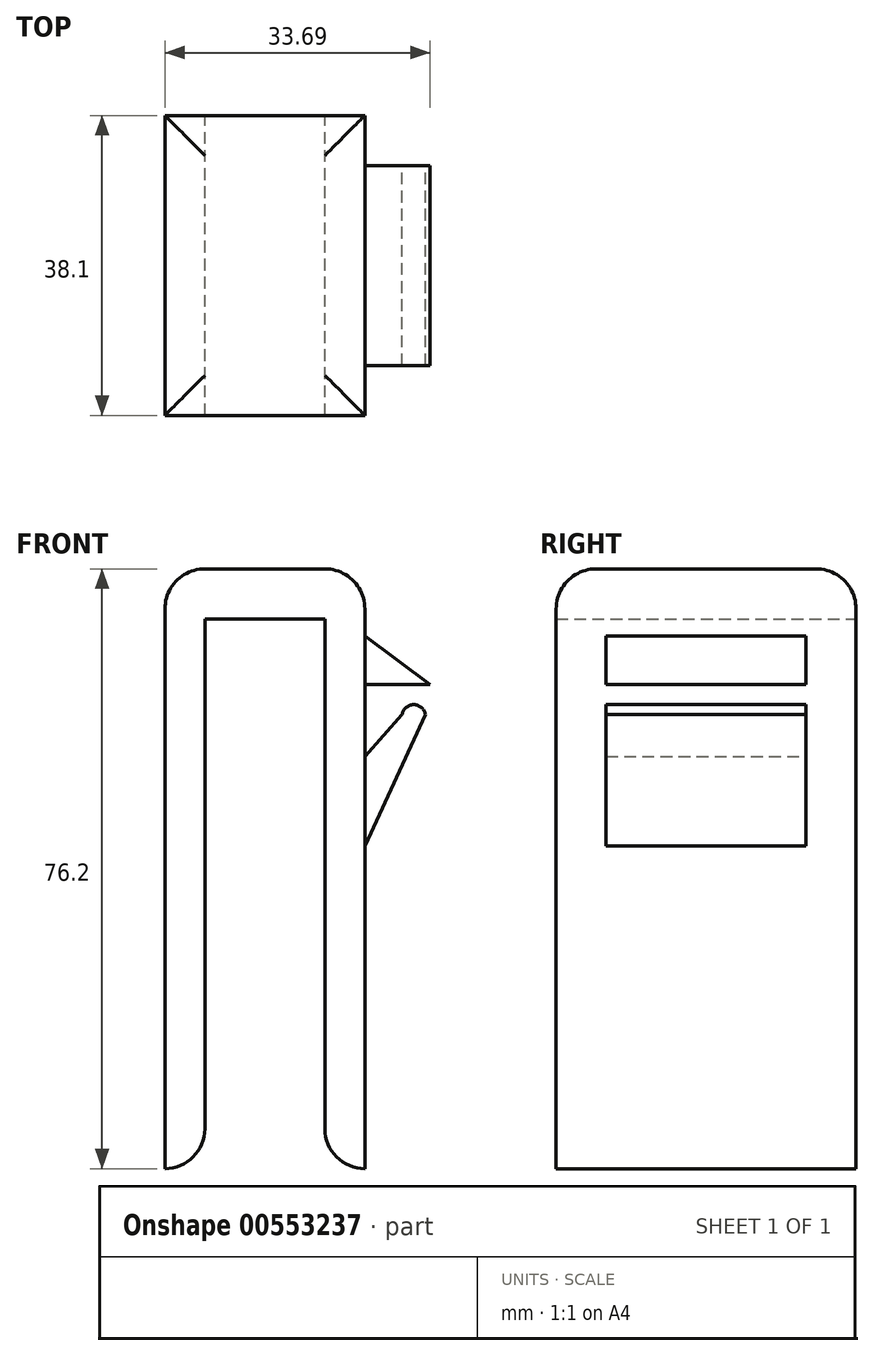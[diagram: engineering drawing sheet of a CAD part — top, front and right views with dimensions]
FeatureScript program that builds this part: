
annotation { "Feature Type Name" : "Feature", "Feature Type Description" : "" }
export const myFeature = defineFeature(function(context is Context, id is Id, definition is map)
    precondition{}
    {
        {
            var Q0;
            Q0=qCreatedBy(makeId("Front.planeOp"),FACE);
            var sketch = newSketch(context, id + "F0", { "sketchPlane" : qUnion([Q0])});
            skLineSegment(sketch, "E0", {"start": v(-8.12, 12.15) * mm, "end": v(7.12, 12.15) * mm});
            skLineSegment(sketch, "E1", {"start": v(-8.12, 12.15) * mm, "end": v(-8.12, -57.7) * mm});
            skLineSegment(sketch, "E2", {"start": v(7.12, 12.15) * mm, "end": v(7.12, -57.7) * mm});
            skLineSegment(sketch, "E3", {"start": v(-8.12, -57.7) * mm, "end": v(-13.2, -57.7) * mm});
            skLineSegment(sketch, "E4", {"start": v(-13.2, -57.7) * mm, "end": v(-13.2, 18.5) * mm});
            skLineSegment(sketch, "E5", {"start": v(-13.2, 18.5) * mm, "end": v(12.2, 18.5) * mm});
            skLineSegment(sketch, "E6", {"start": v(12.2, 18.5) * mm, "end": v(12.2, -57.7) * mm});
            skLineSegment(sketch, "E7", {"start": v(12.2, -57.7) * mm, "end": v(7.12, -57.7) * mm});
            skLineSegment(sketch, "E8", {"start": v(12.2, -5.36) * mm, "end": v(16.92, 0) * mm});
            skLineSegment(sketch, "E9", {"start": v(16.92, 0) * mm, "end": v(19.88, 0) * mm});
            skLineSegment(sketch, "E10", {"start": v(19.88, 0) * mm, "end": v(12.2, -16.68) * mm});
            skLineSegment(sketch, "E11", {"start": v(16.92, 3.81) * mm, "end": v(12.2, 3.8) * mm});
            skLineSegment(sketch, "E12", {"start": v(16.92, 3.8) * mm, "end": v(20.5, 3.8) * mm});
            skLineSegment(sketch, "E13", {"start": v(20.5, 3.81) * mm, "end": v(12.2, 9.99) * mm});
            skArc(sketch, "E14", {"start": v(19.88, 0) * mm, "mid": v(18.4, 1.24) * mm, "end": v(16.92, 0) * mm});
            skSolve(sketch);
        }
        {
            var Q0;
            Q0=makeQuery(id+"F0.imprint","IMPRINT",FACE,{"disambiguationData":[TD([[makeQuery(id+"F0.imprint","IMPRINT",EDGE,{"derivedFrom":sQuery(id+"F0.wireOp",EDGE,"E0")}),1.0]])]});
            extrude(context, id + "F1", {"entities" : qUnion([Q0]), "endBound" : BoundingType.SYMMETRIC, "depth" : 38.1 * mm, "offsetDistance" : 25.4 * mm});
        }
        {
            var Q0;
            {var subQ0=sQuery(id+"F0.wireOp",EDGE,"E11");Q0=makeQuery(id+"F0.imprint","IMPRINT",FACE,{"disambiguationData":[TD([[makeQuery(id+"F0.imprint","IMPRINT",EDGE,{"derivedFrom":subQ0}),-1.0]])]});}
            var Q1;
            {var subQ0=sQuery(id+"F0.wireOp",EDGE,"E8");Q1=makeQuery(id+"F0.imprint","IMPRINT",FACE,{"disambiguationData":[TD([[makeQuery(id+"F0.imprint","IMPRINT",EDGE,{"derivedFrom":subQ0}),-1.0]])]});}
            var Q2;
            Q2=makeQuery(id+"F0.imprint","IMPRINT",FACE,{"disambiguationData":[TD([[makeQuery(id+"F0.imprint","IMPRINT",EDGE,{"derivedFrom":sQuery(id+"F0.wireOp",EDGE,"E9")}),1.0]])]});
            extrude(context, id + "F2", {"entities" : qUnion([Q0, Q1, Q2]), "operationType" : NewBodyOperationType.ADD, "endBound" : BoundingType.SYMMETRIC, "depth" : 25.4 * mm, "offsetDistance" : 25.4 * mm});
        }
        {
            var Q0;
            Q0=makeQuery(id+"F1.opExtrude","SWEPT_EDGE",EDGE,{"disambiguationData":[OSD([sQuery(id+"F0.wireOp",EDGE,"E5"),sQuery(id+"F0.wireOp",EDGE,"E6")])]});
            var Q1;
            Q1=makeQuery(id+"F1.opExtrude","SWEPT_EDGE",EDGE,{"disambiguationData":[OSD([sQuery(id+"F0.wireOp",EDGE,"E4"),sQuery(id+"F0.wireOp",EDGE,"E5")])]});
            var Q2;
            Q2=makeQuery(id+"F1.opExtrude","CAP_EDGE",EDGE,{"disambiguationData":[OSD([sQuery(id+"F0.wireOp",EDGE,"E5")])],"isStart":false});
            var Q3;
            Q3=makeQuery(id+"F1.opExtrude","CAP_EDGE",EDGE,{"disambiguationData":[OSD([sQuery(id+"F0.wireOp",EDGE,"E5")])],"isStart":true});
            var Q4;
            Q4=makeQuery(id+"F1.opExtrude","SWEPT_EDGE",EDGE,{"disambiguationData":[OSD([sQuery(id+"F0.wireOp",EDGE,"E2"),sQuery(id+"F0.wireOp",EDGE,"E7")])]});
            var Q5;
            Q5=makeQuery(id+"F1.opExtrude","SWEPT_EDGE",EDGE,{"disambiguationData":[OSD([sQuery(id+"F0.wireOp",EDGE,"E1"),sQuery(id+"F0.wireOp",EDGE,"E3")])]});
            fillet(context, id + "F3", {"entities" : qUnion([Q0, Q1, Q2, Q3, Q4, Q5]), "radius" : 5.08 * mm, "tangentPropagation" : true, "allowEdgeOverflow" : false});
        }
    });
